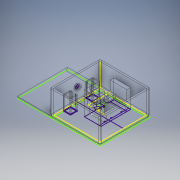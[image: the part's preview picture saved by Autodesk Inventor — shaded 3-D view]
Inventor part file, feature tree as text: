
AUTODESK INVENTOR PART (.ipt)
format: ipt  version: 2019 (Build 230136000, 136)  size: 382,464 bytes
history: native  units: in
note: dims shown in document units (in); Inventor stores cm internally (conversion verified against a paired STEP export)
features: extrude x25, sketch x22, fillet x2, other x1
ambient origin geometry x8: Origin, YZ Plane, XZ Plane, XY Plane, X Axis, Y Axis, Z Axis, Center Point
bodies: Solid1 (feature_tree)
feature tree (50):
  other  "ohisje"
  extrude  "Extrusion1"  Depth=1.9685in
  extrude  "Extrusion2"  Depth=0.0787in
  fillet  "Fillet1"  Radius=0.0787in
  sketch  "Sketch3"  dims[d5=0.0787in d6=1.378in]
  extrude  "Extrusion3"  Depth=1.378in
  sketch  "Sketch4"  dims[d7=2.126in d8=1.063in d9=0.0in d10=0.0787in]
  extrude  "Extrusion4"  Depth=1.063in TaperAngle=0.0deg
  fillet  "Fillet2"  Radius=0.0787in
  extrude  "Extrusion5"  Depth=0.0787in
  extrude  "Extrusion6"  Depth=0.315in
  extrude  "Extrusion7"  Depth=0.2402in
  sketch  "Sketch8"  dims[d30=0.0374in d31=0.0374in]
  extrude  "Extrusion8"  Depth=0.0374in
  extrude  "Extrusion9"  Depth=0.9843in
  extrude  "Extrusion10"  Depth=0.5906in TaperAngle=0.0deg
  extrude  "Extrusion11"  Depth=0.0394in
  extrude  "Extrusion12"  Depth=0.9843in
  sketch  "Sketch14"  dims[d46=0.1181in d47=1.2598in]
  extrude  "Extrusion13"  Depth=0.0394in TaperAngle=0.0deg
  extrude  "Extrusion14"  Depth=1.2598in
  extrude  "Extrusion16"  Depth=0.5512in TaperAngle=0.0deg
  extrude  "Extrusion17"  Depth=0.5512in TaperAngle=0.0deg
  extrude  "Extrusion18"  Depth=0.4724in
  extrude  "Extrusion19"  Depth=0.3937in TaperAngle=0.0deg
  extrude  "Extrusion20"  Depth=0.0374in
  extrude  "Extrusion21"  Depth=0.0374in
  sketch  "Sketch18"  dims[d54=0.5512in d55=0.4724in]
  sketch  "Sketch19"  dims[d56=0.0394in d57=0.3937in d58=0.0in]
  extrude  "Extrusion22"  Depth=0.0374in
  extrude  "Extrusion23"  Depth=0.2362in
  sketch  "Sketch20"  dims[d59=0.0374in d60=0.0374in]
  extrude  "Extrusion24"  Depth=0.0787in TaperAngle=0.0deg
  extrude  "Extrusion25"  Depth=0.3937in
  extrude  "Extrusion26"  Depth=0.1969in TaperAngle=0.0deg
  sketch  "Sketch1"  dims[d0=1.9685in d1=1.9685in]
  sketch  "Sketch2"  dims[d2=0.0787in d3=0.0787in d4=0.0787in]
  sketch  "Sketch5"  dims[d11=3.5039in d12=0.0in d13=0.0787in]
  sketch  "Sketch6"  dims[d26=0.3543in d27=0.315in]
  sketch  "Sketch7"  dims[d28=0.0394in d29=0.2402in]
  sketch  "Sketch9"  dims[d33=0.9843in d34=0.9843in]
  sketch  "Sketch10"  dims[d35=0.5906in d36=0.0in d37=0.5906in d38=0.0in]
  sketch  "Sketch11"  dims[d39=0.6299in d40=0.0394in]
  sketch  "Sketch12"  dims[d41=0.1417in d42=0.9843in]
  sketch  "Sketch13"  dims[d43=0.5512in d44=0.0394in d45=0.0in]
  sketch  "Sketch15"  dims[d48=0.0591in d49=0.5512in d50=0.0in]
  sketch  "Sketch17"  dims[d51=0.1417in d52=0.5512in d53=0.0in]
  sketch  "Sketch21"  dims[d61=0.3937in d62=0.0in d63=0.0374in]
  sketch  "Sketch22"  dims[d64=0.0374in d65=0.0374in]
  sketch  "Sketch23"  dims[d66=0.3937in d67=0.0in d68=0.2362in d69=0.0787in d70=0.0in d71=0.3937in d72=0.1969in d73=0.0in d74=0.8661in d75=0.7087in d76=0.7087in d77=0.3937in d78=0.7087in d79=0.3543in d80=0.0in d81=0.1575in d82=0.6299in d83=0.0in d87=0.1575in d88=0.7874in d89=0.0in d90=0.0787in d91=0.9449in d92=0.0in d93=0.2362in d94=0.0394in d95=0.0394in d96=0.1181in d97=0.1181in d98=0.0394in d99=0.0394in d100=0.3937in d101=0.0394in d102=0.0394in d103=0.9449in d104=0.0in d105=0.9449in d106=0.0in d107=0.9449in d108=0.0in d109=0.2362in d110=0.4724in d111=0.0in d112=0.3543in d113=0.1181in d114=0.1575in d115=0.1181in d116=0.1575in d117=0.3937in d118=0.0in d119=0.1181in d120=0.0in d121=0.1181in d122=0.1575in d123=0.0in d124=0.0787in d125=0.2756in d126=0.8268in d127=0.7874in d128=0.0in d129=0.0591in d130=0.1181in d131=0.3937in d132=0.0in d133=0.1575in]
